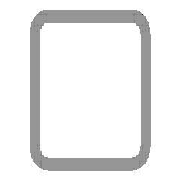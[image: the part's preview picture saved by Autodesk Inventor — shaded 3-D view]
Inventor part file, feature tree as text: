
AUTODESK INVENTOR PART (.ipt)
format: ipt  version: 2025.1 (Build 291241020, 241B)  size: 133,632 bytes
history: native  units: mm (DEFAULTED — no unit token found)
features: other x4, sketch x1, plane x1
ambient origin geometry x8: Origin, YZ Plane, XZ Plane, XY Plane, X Axis, Y Axis, Z Axis, Center Point
bodies: Solid1 (feature_tree), Body (feature_tree)
feature tree (6):
  parser-record x1  (decoder bookkeeping rows leaked as tree rows — omitted from the tree; the rows remain in map.json)
  other  "Driven Length"
  other  "Start Plane"
  other  "End Plane"
  sketch  "Sketch3"  dims[d3=610.0mm d4=0.0mm d7=4.0mm d9=40.0mm d11=40.0mm d12=2.0mm d13=20.0mm d14=630.0mm d15=20.0mm d16=20.0mm d17=90.0deg d18=610.0mm]
  plane  "Work Plane3"
